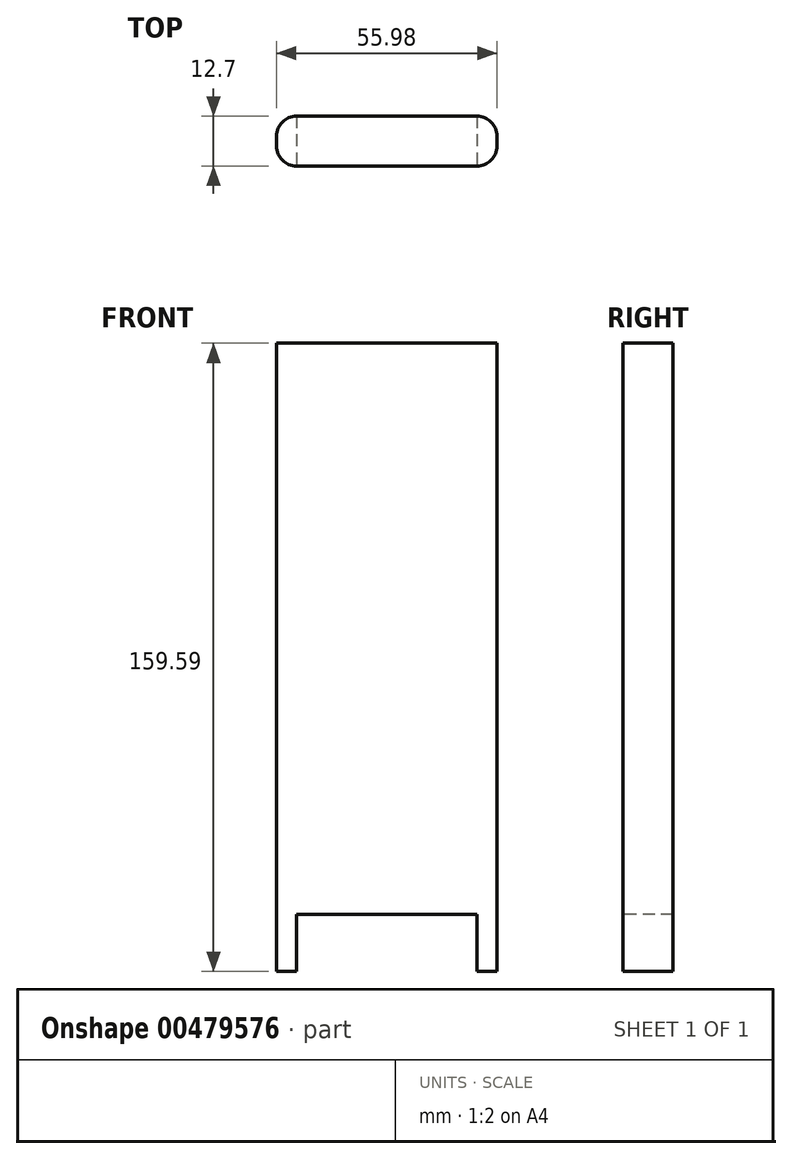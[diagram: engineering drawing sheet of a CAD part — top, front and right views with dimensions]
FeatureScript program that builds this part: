
annotation { "Feature Type Name" : "Feature", "Feature Type Description" : "" }
export const myFeature = defineFeature(function(context is Context, id is Id, definition is map)
    precondition{}
    {
        {
            var Q0;
            Q0=qCreatedBy(makeId("Front.planeOp"),FACE);
            var sketch = newSketch(context, id + "F0", { "sketchPlane" : qUnion([Q0])});
            skLineSegment(sketch, "E0.bottom", {"start": v(-28, -51.37) * mm, "end": v(28, -51.37) * mm});
            skLineSegment(sketch, "E0.top", {"start": v(-28, 51.37) * mm, "end": v(28, 51.37) * mm});
            skLineSegment(sketch, "E0.left", {"start": v(-28, -51.37) * mm, "end": v(-28, 51.37) * mm});
            skLineSegment(sketch, "E0.right", {"start": v(28, -51.37) * mm, "end": v(28, 51.37) * mm});
            skPoint(sketch, "E0.middle", {"position": v(0, 0) * mm});
            skSolve(sketch);
        }
        {
            var Q0;
            Q0 = qSketchRegion(id + "F0", true);
            extrude(context, id + "F1", {"entities" : qUnion([Q0]), "depth" : 12.7 * mm});
        }
        {
            var Q0;
            Q0=makeQuery(id+"F1.opExtrude","CAP_EDGE",EDGE,{"disambiguationData":[OSD([sQuery(id+"F0.wireOp",EDGE,"E0.right")])],"isStart":false});
            var Q1;
            Q1=makeQuery(id+"F1.opExtrude","CAP_EDGE",EDGE,{"disambiguationData":[OSD([sQuery(id+"F0.wireOp",EDGE,"E0.right")])],"isStart":true});
            var Q2;
            Q2=makeQuery(id+"F1.opExtrude","CAP_EDGE",EDGE,{"disambiguationData":[OSD([sQuery(id+"F0.wireOp",EDGE,"E0.left")])],"isStart":false});
            var Q3;
            Q3=makeQuery(id+"F1.opExtrude","CAP_EDGE",EDGE,{"disambiguationData":[OSD([sQuery(id+"F0.wireOp",EDGE,"E0.left")])],"isStart":true});
            fillet(context, id + "F2", {"entities" : qUnion([Q0, Q1, Q2, Q3]), "radius" : 5.08 * mm, "tangentPropagation" : true, "allowEdgeOverflow" : false});
        }
        {
            var Q0;
            Q0=makeQuery(id+"F1.opExtrude","CAP_FACE",FACE,{"disambiguationData":[OSD([sQuery(id+"F0.wireOp",EDGE,"E0.bottom"),sQuery(id+"F0.wireOp",EDGE,"E0.top"),sQuery(id+"F0.wireOp",EDGE,"E0.left"),sQuery(id+"F0.wireOp",EDGE,"E0.right")])],"isStart":false});
            var sketch = newSketch(context, id + "F3", { "sketchPlane" : qUnion([Q0])});
            skLineSegment(sketch, "E1.bottom", {"start": v(-22.91, -51.37) * mm, "end": v(22.91, -51.37) * mm});
            skLineSegment(sketch, "E1.top", {"start": v(-22.91, -36.94) * mm, "end": v(22.91, -36.94) * mm});
            skLineSegment(sketch, "E1.left", {"start": v(-22.91, -51.37) * mm, "end": v(-22.91, -36.94) * mm});
            skLineSegment(sketch, "E1.right", {"start": v(22.91, -51.37) * mm, "end": v(22.91, -36.94) * mm});
            skSolve(sketch);
        }
        {
            var Q0;
            Q0=makeQuery(id+"F3.imprint","IMPRINT",FACE,{"disambiguationData":[TD([[makeQuery(id+"F3.imprint","IMPRINT",EDGE,{"derivedFrom":sQuery(id+"F3.wireOp",EDGE,"E1.bottom")}),1.0]])]});
            extrude(context, id + "F4", {"entities" : qUnion([Q0]), "operationType" : NewBodyOperationType.REMOVE, "oppositeDirection" : true, "depth" : 25.4 * mm});
        }
        {
            var Q0;
            Q0=makeQuery(id+"F1.opExtrude","CAP_FACE",FACE,{"disambiguationData":[OSD([sQuery(id+"F0.wireOp",EDGE,"E0.bottom"),sQuery(id+"F0.wireOp",EDGE,"E0.top"),sQuery(id+"F0.wireOp",EDGE,"E0.left"),sQuery(id+"F0.wireOp",EDGE,"E0.right")])],"isStart":false});
            var sketch = newSketch(context, id + "F5", { "sketchPlane" : qUnion([Q0])});
            skArc(sketch, "E2", {"start": v(0, 102.03) * mm, "mid": v(-16.92, 79.17) * mm, "end": v(-22.91, 51.37) * mm});
            skSolve(sketch);
        }
        {
            var Q0;
            {var subQ0=sQuery(id+"F0.wireOp",EDGE,"E0.top");Q0=makeQuery(id+"F5.imprint","IMPRINT",FACE,{"disambiguationData":[TD([[makeQuery(id+"F5.imprint","IMPRINT",EDGE,{"derivedFrom":makeQuery(id+"F1.opExtrude","CAP_EDGE",EDGE,{"disambiguationData":[OSD([subQ0])],"isStart":false})}),-1.0]])]});}
            var sketch = newSketch(context, id + "F6", { "sketchPlane" : qUnion([Q0])});
            skSolve(sketch);
        }
        {
            var Q0;
            {var subQ0=sQuery(id+"F0.wireOp",EDGE,"E0.top");Q0=makeQuery(id+"F5.imprint","IMPRINT",FACE,{"disambiguationData":[TD([[makeQuery(id+"F5.imprint","IMPRINT",EDGE,{"derivedFrom":makeQuery(id+"F1.opExtrude","CAP_EDGE",EDGE,{"disambiguationData":[OSD([subQ0])],"isStart":false})}),-1.0]])]});}
            var sketch = newSketch(context, id + "F7", { "sketchPlane" : qUnion([Q0])});
            skArc(sketch, "E3", {"start": v(23.26, 51.01) * mm, "mid": v(17.72, 79.42) * mm, "end": v(0, 102.32) * mm});
            skSolve(sketch);
        }
        {
            var Q0;
            Q0=makeQuery(id+"F1.opExtrude","SWEPT_FACE",FACE,{"disambiguationData":[OSD([sQuery(id+"F0.wireOp",EDGE,"E0.top")])]});
            var Q1;
            Q1=sQuery(id+"F7.wireOp",EDGE,"E3");
            var Q2;
            Q2=sQuery(id+"F5.wireOp",EDGE,"E2");
            extrude(context, id + "F8", {"entities" : qUnion([Q0]), "operationType" : NewBodyOperationType.ADD, "surfaceEntities" : qUnion([Q1, Q2]), "depth" : 56.84 * mm});
        }
    });
